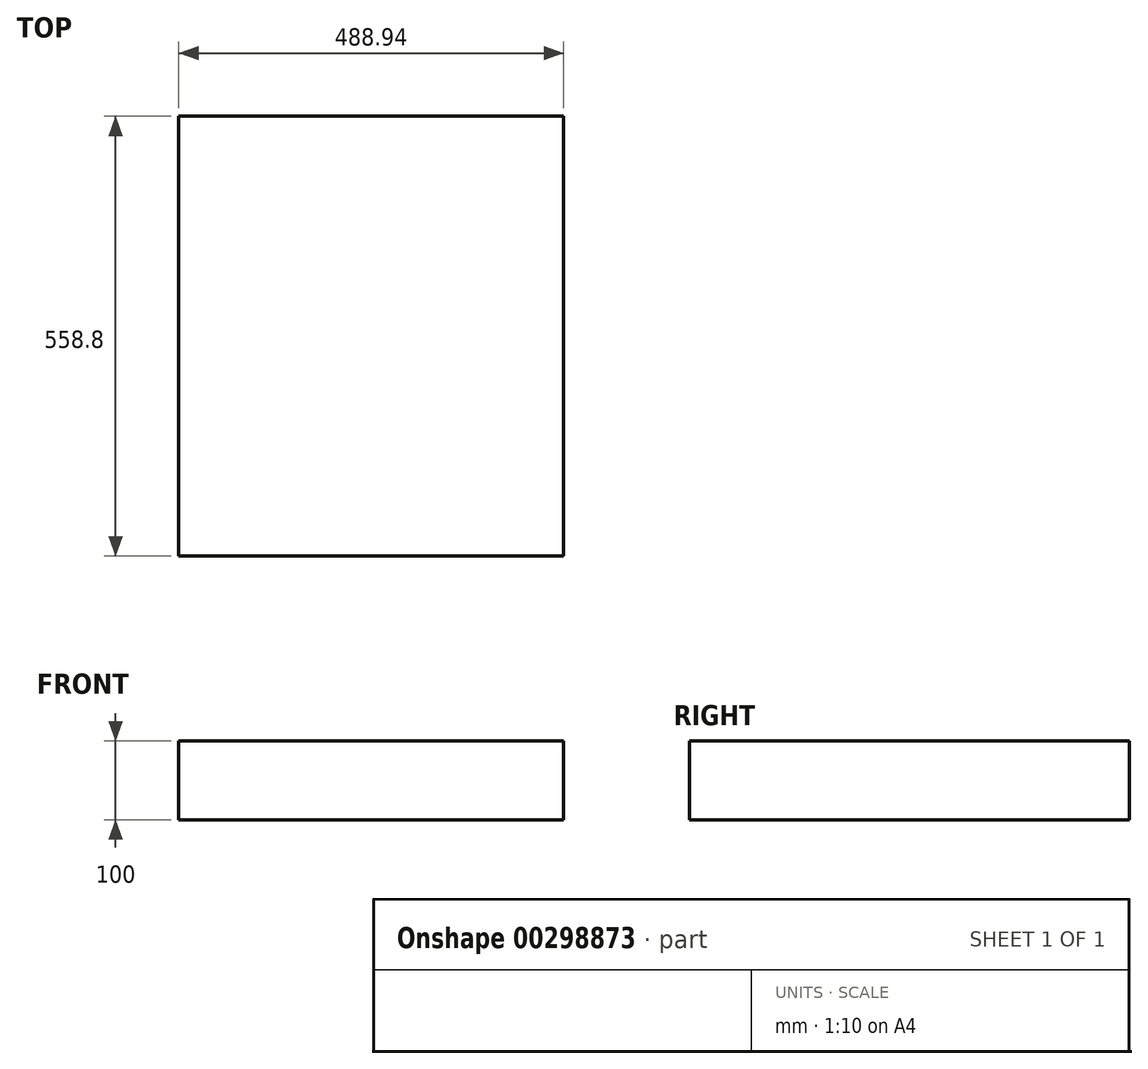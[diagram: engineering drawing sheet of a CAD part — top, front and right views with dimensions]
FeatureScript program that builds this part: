
annotation { "Feature Type Name" : "Feature", "Feature Type Description" : "" }
export const myFeature = defineFeature(function(context is Context, id is Id, definition is map)
    precondition{}
    {
        {
            var Q0;
            Q0=qCreatedBy(makeId("Top.planeOp"),FACE);
            var sketch = newSketch(context, id + "F0", { "sketchPlane" : qUnion([Q0])});
            skLineSegment(sketch, "E0.bottom", {"start": v(244.48, -279.4) * mm, "end": v(-244.47, -279.4) * mm});
            skLineSegment(sketch, "E0.top", {"start": v(244.47, 279.4) * mm, "end": v(-244.48, 279.4) * mm});
            skLineSegment(sketch, "E0.left", {"start": v(244.48, -279.4) * mm, "end": v(244.47, 279.4) * mm});
            skLineSegment(sketch, "E0.right", {"start": v(-244.47, -279.4) * mm, "end": v(-244.48, 279.4) * mm});
            skPoint(sketch, "E0.middle", {"position": v(0, 0) * mm});
            skSolve(sketch);
        }
        {
            var Q0;
            Q0 = qSketchRegion(id + "F0", true);
            extrude(context, id + "F1", {"entities" : qUnion([Q0]), "depth" : 100 * mm});
        }
    });
